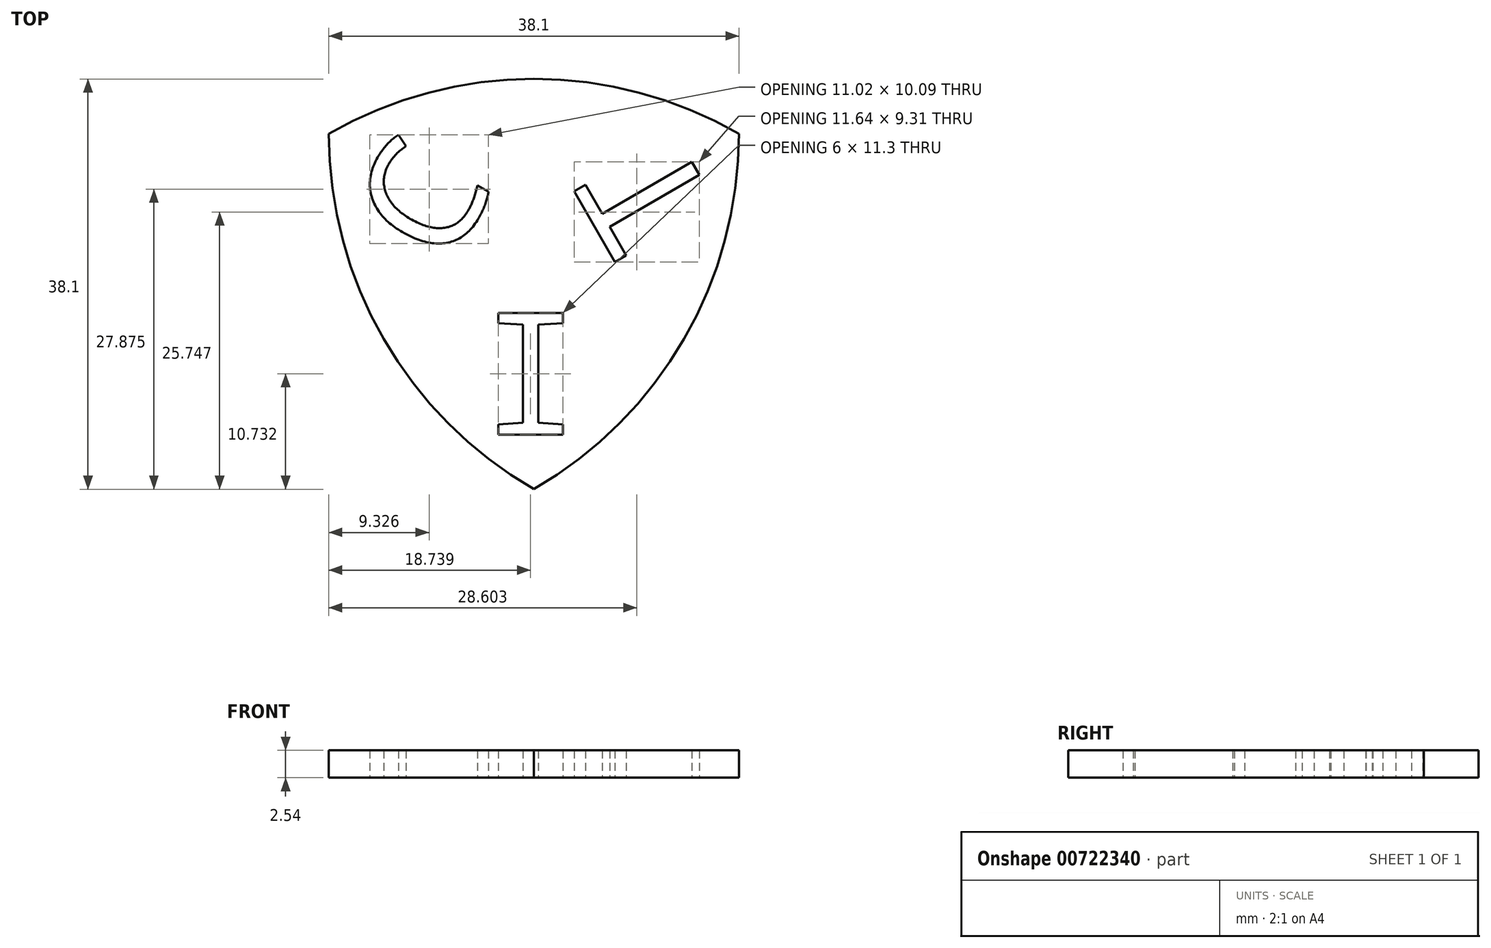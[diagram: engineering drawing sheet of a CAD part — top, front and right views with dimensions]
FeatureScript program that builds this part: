
annotation { "Feature Type Name" : "Feature", "Feature Type Description" : "" }
export const myFeature = defineFeature(function(context is Context, id is Id, definition is map)
    precondition{}
    {
        {
            var Q0;
            Q0=qCreatedBy(makeId("Top.planeOp"),FACE);
            var sketch = newSketch(context, id + "F0", { "sketchPlane" : qUnion([Q0])});
            skCircle(sketch, "E0", {"center": v(0, 0) * mm, "radius": 38.1 * mm});
            skSolve(sketch);
        }
        {
            var Q0;
            Q0=qCreatedBy(makeId("Top.planeOp"),FACE);
            var sketch = newSketch(context, id + "F1", { "sketchPlane" : qUnion([Q0])});
            skCircle(sketch, "E1", {"center": v(-38.1, 0) * mm, "radius": 38.1 * mm});
            skSolve(sketch);
        }
        {
            var Q0;
            Q0=qCreatedBy(makeId("Top.planeOp"),FACE);
            var sketch = newSketch(context, id + "F2", { "sketchPlane" : qUnion([Q0])});
            skCircle(sketch, "E2", {"center": v(-19.05, -33) * mm, "radius": 38.1 * mm});
            skSolve(sketch);
        }
        {
            var Q0;
            Q0=makeQuery(id+"F0.imprint","IMPRINT",FACE,{"disambiguationData":[TD([[makeQuery(id+"F0.imprint","IMPRINT",EDGE,{"derivedFrom":sQuery(id+"F0.wireOp",EDGE,"E0")}),1.0]])]});
            extrude(context, id + "F3", {"entities" : qUnion([Q0]), "depth" : 2.54 * mm, "offsetDistance" : 25.4 * mm});
        }
        {
            var Q0;
            Q0=makeQuery(id+"F1.imprint","IMPRINT",FACE,{"disambiguationData":[TD([[makeQuery(id+"F1.imprint","IMPRINT",EDGE,{"derivedFrom":sQuery(id+"F1.wireOp",EDGE,"E1")}),1.0]])]});
            extrude(context, id + "F4", {"entities" : qUnion([Q0]), "depth" : 2.54 * mm, "offsetDistance" : 25.4 * mm});
        }
        {
            var Q0;
            Q0=makeQuery(id+"F2.imprint","IMPRINT",FACE,{"disambiguationData":[TD([[makeQuery(id+"F2.imprint","IMPRINT",EDGE,{"derivedFrom":sQuery(id+"F2.wireOp",EDGE,"E2")}),1.0]])]});
            extrude(context, id + "F5", {"entities" : qUnion([Q0]), "depth" : 2.54 * mm, "offsetDistance" : 25.4 * mm});
        }
        {
            var Q0;
            Q0=makeQuery(id+"F3.opExtrude","SWEPT_BODY",BODY,{"disambiguationData":[OSD([sQuery(id+"F0.wireOp",EDGE,"E0")])]});
            var Q1;
            Q1=makeQuery(id+"F4.opExtrude","SWEPT_BODY",BODY,{"disambiguationData":[OSD([sQuery(id+"F1.wireOp",EDGE,"E1")])]});
            var Q2;
            Q2=makeQuery(id+"F5.opExtrude","SWEPT_BODY",BODY,{"disambiguationData":[OSD([sQuery(id+"F2.wireOp",EDGE,"E2")])]});
            booleanBodies(context, id + "F6", {"operationType" : BooleanOperationType.INTERSECTION, "tools" : qUnion([Q0, Q1, Q2])});
        }
        {
            var Q0;
            Q0=qCreatedBy(makeId("Top.planeOp"),FACE);
            var sketch = newSketch(context, id + "F7", { "sketchPlane" : qUnion([Q0])});
            skText(sketch, "E3", { "text": "C", "fontName": "DroidSansMono.ttf"});
            skText(sketch, "E4", { "text": "I", "fontName": "DroidSansMono.ttf"});
            skText(sketch, "E5", { "text": "T", "fontName": "DroidSansMono.ttf"});
            const initialGuessF7  = {"E3": [-0.02711, -0.0126, 0.5, 0.86603, 0.01073], "E4": [-0.0241, -0.02792, 1, 0, 0.0114], "E5": [-0.00175, -0.00714, -0.5, 0.86603, 0.01094]};
            skSetInitialGuess(sketch, initialGuessF7);
            skSolve(sketch);
        }
        {
            var Q0;
            Q0 = qSketchRegion(id + "F7", true);
            extrude(context, id + "F8", {"entities" : qUnion([Q0]), "depth" : 2.54 * mm, "offsetDistance" : 25.4 * mm});
        }
        {
            var Q0;
            Q0=makeQuery(id+"F8.opExtrude","SWEPT_BODY",BODY,{"disambiguationData":[OSD([sQuery(id+"F7.wireOp",EDGE,"E3.sketch_text.stroke-0"),sQuery(id+"F7.wireOp",EDGE,"E3.sketch_text.stroke-1"),sQuery(id+"F7.wireOp",EDGE,"E3.sketch_text.stroke-2"),sQuery(id+"F7.wireOp",EDGE,"E3.sketch_text.stroke-3"),sQuery(id+"F7.wireOp",EDGE,"E3.sketch_text.stroke-4"),sQuery(id+"F7.wireOp",EDGE,"E3.sketch_text.stroke-5"),sQuery(id+"F7.wireOp",EDGE,"E3.sketch_text.stroke-6"),sQuery(id+"F7.wireOp",EDGE,"E3.sketch_text.stroke-7"),sQuery(id+"F7.wireOp",EDGE,"E3.sketch_text.stroke-8"),sQuery(id+"F7.wireOp",EDGE,"E3.sketch_text.stroke-9"),sQuery(id+"F7.wireOp",EDGE,"E3.sketch_text.stroke-10"),sQuery(id+"F7.wireOp",EDGE,"E3.sketch_text.stroke-11"),sQuery(id+"F7.wireOp",EDGE,"E3.sketch_text.stroke-12"),sQuery(id+"F7.wireOp",EDGE,"E3.sketch_text.stroke-13")])]});
            var Q1;
            Q1=makeQuery(id+"F8.opExtrude","SWEPT_BODY",BODY,{"disambiguationData":[OSD([sQuery(id+"F7.wireOp",EDGE,"E5.sketch_text.stroke-0"),sQuery(id+"F7.wireOp",EDGE,"E5.sketch_text.stroke-1"),sQuery(id+"F7.wireOp",EDGE,"E5.sketch_text.stroke-2"),sQuery(id+"F7.wireOp",EDGE,"E5.sketch_text.stroke-3"),sQuery(id+"F7.wireOp",EDGE,"E5.sketch_text.stroke-4"),sQuery(id+"F7.wireOp",EDGE,"E5.sketch_text.stroke-5"),sQuery(id+"F7.wireOp",EDGE,"E5.sketch_text.stroke-6"),sQuery(id+"F7.wireOp",EDGE,"E5.sketch_text.stroke-7")])]});
            var Q2;
            Q2=makeQuery(id+"F8.opExtrude","SWEPT_BODY",BODY,{"disambiguationData":[OSD([sQuery(id+"F7.wireOp",EDGE,"E4.sketch_text.stroke-0"),sQuery(id+"F7.wireOp",EDGE,"E4.sketch_text.stroke-1"),sQuery(id+"F7.wireOp",EDGE,"E4.sketch_text.stroke-2"),sQuery(id+"F7.wireOp",EDGE,"E4.sketch_text.stroke-3"),sQuery(id+"F7.wireOp",EDGE,"E4.sketch_text.stroke-4"),sQuery(id+"F7.wireOp",EDGE,"E4.sketch_text.stroke-5"),sQuery(id+"F7.wireOp",EDGE,"E4.sketch_text.stroke-6"),sQuery(id+"F7.wireOp",EDGE,"E4.sketch_text.stroke-7"),sQuery(id+"F7.wireOp",EDGE,"E4.sketch_text.stroke-8"),sQuery(id+"F7.wireOp",EDGE,"E4.sketch_text.stroke-9"),sQuery(id+"F7.wireOp",EDGE,"E4.sketch_text.stroke-10"),sQuery(id+"F7.wireOp",EDGE,"E4.sketch_text.stroke-11")])]});
            var Q3;
            Q3=makeQuery(id+"F6.opBoolean","INTERSECT",BODY,{"derivedFrom":[makeQuery(id+"F3.opExtrude","SWEPT_BODY",BODY,{"disambiguationData":[OSD([sQuery(id+"F0.wireOp",EDGE,"E0")])]}),makeQuery(id+"F4.opExtrude","SWEPT_BODY",BODY,{"disambiguationData":[OSD([sQuery(id+"F1.wireOp",EDGE,"E1")])]}),makeQuery(id+"F5.opExtrude","SWEPT_BODY",BODY,{"disambiguationData":[OSD([sQuery(id+"F2.wireOp",EDGE,"E2")])]})]});
            booleanBodies(context, id + "F9", {"operationType" : BooleanOperationType.SUBTRACTION, "tools" : qUnion([Q0, Q1, Q2]), "targets" : qUnion([Q3])});
        }
    });
